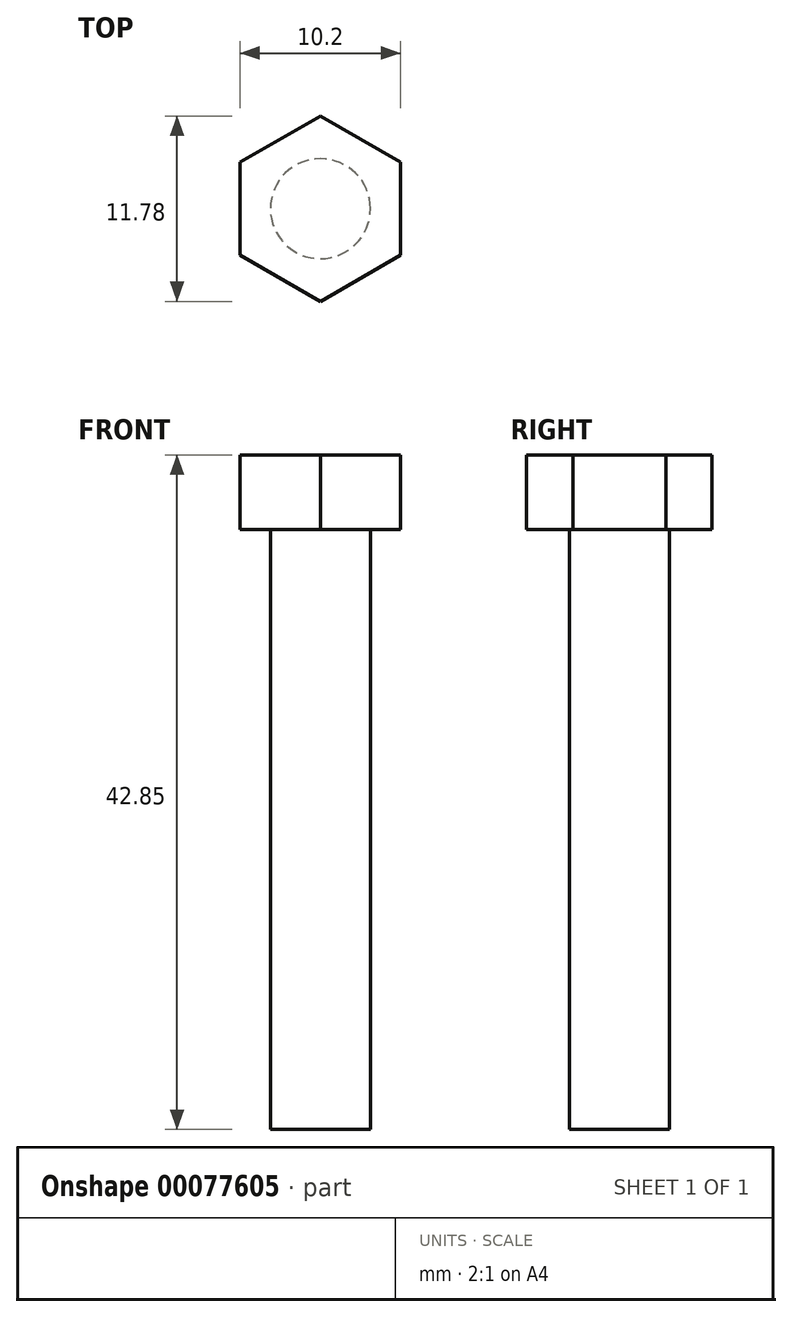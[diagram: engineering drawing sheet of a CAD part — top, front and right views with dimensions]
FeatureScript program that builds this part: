
annotation { "Feature Type Name" : "Feature", "Feature Type Description" : "" }
export const myFeature = defineFeature(function(context is Context, id is Id, definition is map)
    precondition{}
    {
        {
            var Q0;
            Q0=qCreatedBy(makeId("Top.planeOp"),FACE);
            var sketch = newSketch(context, id + "F0", { "sketchPlane" : qUnion([Q0])});
            skCircle(sketch, "E0", {"center": v(0, 0) * mm, "radius": 3.17 * mm});
            skSolve(sketch);
        }
        {
            var Q0;
            Q0 = qSketchRegion(id + "F0", true);
            extrude(context, id + "F1", {"entities" : qUnion([Q0]), "oppositeDirection" : true, "depth" : 38.1 * mm});
        }
        {
            var Q0;
            Q0=makeQuery(id+"F1.opExtrude","CAP_FACE",FACE,{"disambiguationData":[OSD([sQuery(id+"F0.wireOp",EDGE,"E0")])],"isStart":true});
            var sketch = newSketch(context, id + "F2", { "sketchPlane" : qUnion([Q0])});
            skCircle(sketch, "E1.cCircle", {"center": v(0, 0) * mm, "radius": 5.89 * mm, "construction": true});
            skLineSegment(sketch, "E1.0", {"start": v(0, 5.89) * mm, "end": v(5.1, 2.94) * mm});
            skLineSegment(sketch, "E1.1", {"start": v(5.1, 2.94) * mm, "end": v(5.1, -2.94) * mm});
            skLineSegment(sketch, "E1.2", {"start": v(5.1, -2.94) * mm, "end": v(0, -5.89) * mm});
            skLineSegment(sketch, "E1.3", {"start": v(0, -5.89) * mm, "end": v(-5.1, -2.94) * mm});
            skLineSegment(sketch, "E1.4", {"start": v(-5.1, -2.94) * mm, "end": v(-5.1, 2.94) * mm});
            skLineSegment(sketch, "E1.5", {"start": v(-5.1, 2.94) * mm, "end": v(0, 5.89) * mm});
            skSolve(sketch);
        }
        {
            var Q0;
            Q0 = qSketchRegion(id + "F2", true);
            extrude(context, id + "F3", {"entities" : qUnion([Q0]), "operationType" : NewBodyOperationType.ADD, "depth" : 4.75 * mm});
        }
    });
